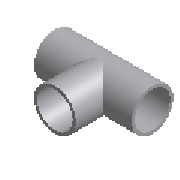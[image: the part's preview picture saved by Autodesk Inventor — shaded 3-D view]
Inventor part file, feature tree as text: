
AUTODESK INVENTOR PART (.ipt)
format: ipt  version: 2025.1 (Build 291241020, 241B)  size: 169,472 bytes
history: native  units: mm (DEFAULTED — no unit token found)
features: other x6, extrude x4
ambient origin geometry x8: Origin, YZ Plane, XZ Plane, XY Plane, X Axis, Y Axis, Z Axis, Center Point
bodies: Solid1 (feature_tree)
feature tree (10):
  extrude  "Extrude1"  Depth=60.3mm
  extrude  "Extrude2"  Depth=128.0mm
  extrude  "Extrude3"  TaperAngle=0.0deg  [1 undecoded]
  extrude  "Extrude4"  Depth=60.3mm
  other  "Work Axis1"
  other  "Work Point1"
  other  "Work Axis2"
  other  "Work Point2"
  other  "Work Axis3"
  other  "Work Point3"
note: 1 required parameter value undecoded (feature->parameter linkage not recoverable at this tier; creation-order binding heuristic only, values carry confidence <= 0.55)
